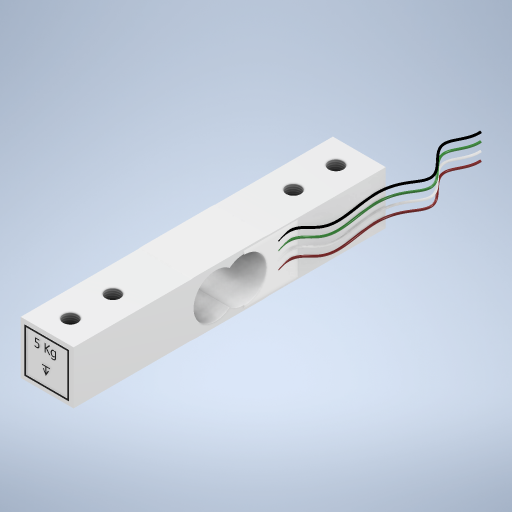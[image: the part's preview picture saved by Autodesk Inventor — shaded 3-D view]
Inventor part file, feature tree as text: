
AUTODESK INVENTOR PART (.ipt)
format: ipt  version: 2024 (Build 280153000, 153)  size: 709,120 bytes
history: native  units: mm
features: sketch x7, extrude x5, thread x4, plane x2, fillet x2, mirror x1, sweep x1, pattern_linear x1, projected_geometry x1
ambient origin geometry x8: Origin, YZ Plane, XZ Plane, XY Plane, X Axis, Y Axis, Z Axis, Center Point
bodies: Solid1 (feature_tree)
feature tree (24):
  extrude  "Extrusion1"  Depth=12.7mm
  extrude  "Extrusion2"  Depth=10.6mm
  thread  "Thread1"  [1 undecoded]
  thread  "Thread2"  [1 undecoded]
  thread  "Thread3"  [1 undecoded]
  thread  "Thread4"  [1 undecoded]
  extrude  "Extrusion3"  Depth=3.5mm
  extrude  "Extrusion4"  Depth=3.5mm
  plane  "Work Plane1"
  mirror  "Mirror1"
  fillet  "Fillet1"  Radius=3.5mm
  sketch  "3D Sketch1"
  plane  "Work Plane2"
  sweep  "Sweep1"
  pattern_linear  "Rectangular Pattern1"  Spacing1=12.7mm  [1 undecoded]
  extrude  "Extrusion5"  Depth=2.0mm TaperAngle=0.0deg
  fillet  "Fillet2"  Radius=12.7mm
  sketch  "Sketch1"  dims[d0=75.0mm d1=12.7mm]
  sketch  "Sketch2"  dims[d2=10.6mm d3=10.6mm d4=8.2mm d5=5.3mm d6=5.3mm d7=12.7mm d8=0.0mm]
  sketch  "Sketch3"  dims[d9=5.6mm d10=3.5mm]
  projected_geometry  "Projected Loop1"
  sketch  "Sketch4"  dims[d11=3.5mm d12=3.5mm d13=3.5mm]
  sketch  "Sketch5"  dims[d15=10.2mm d16=10.2mm]
  sketch  "Sketch6"  dims[d17=5.6mm d18=12.7mm d19=0.0mm d20=12.7mm d21=0.0mm d22=12.7mm d23=0.0mm d24=12.7mm d25=0.0mm d26=12.7mm d27=0.0mm d30=1.0mm d31=1.0mm d32=0.4mm d33=1.0mm d34=1.0mm d35=0.1mm d36=0.0mm d37=18.5mm d38=0.1mm d39=0.0mm d40=10.0mm d41=0.5mm d42=0.0mm d43=0.0mm d44=40.0mm d46=2.0mm d47=12.0mm d48=13.0mm d49=0.2mm d50=0.0mm d51=2.0mm]
note: 5 required parameter values undecoded (feature->parameter linkage not recoverable at this tier; creation-order binding heuristic only, values carry confidence <= 0.55)
